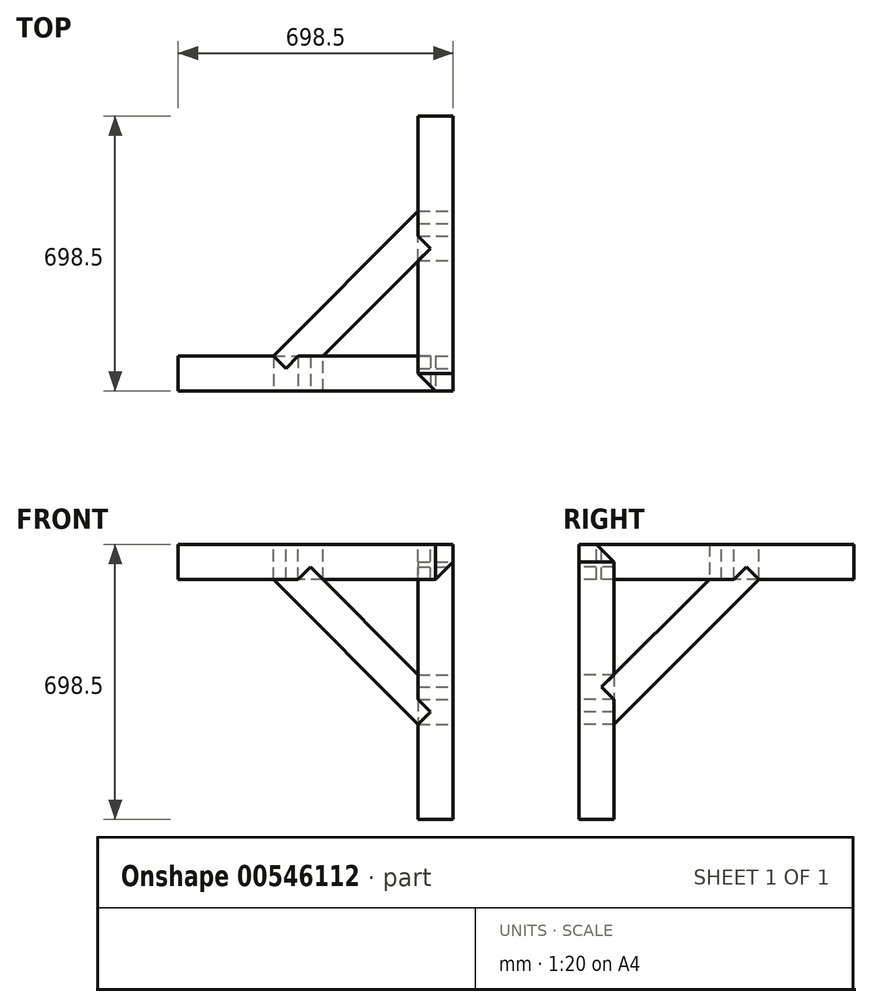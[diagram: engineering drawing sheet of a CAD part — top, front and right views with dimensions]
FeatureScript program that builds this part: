
annotation { "Feature Type Name" : "Feature", "Feature Type Description" : "" }
export const myFeature = defineFeature(function(context is Context, id is Id, definition is map)
    precondition{}
    {
        {
            var Q0;
            Q0=qCreatedBy(makeId("Top.planeOp"),FACE);
            var sketch = newSketch(context, id + "F0", { "sketchPlane" : qUnion([Q0])});
            skLineSegment(sketch, "E0.bottom", {"start": v(0, 0) * mm, "end": v(88.9, 0) * mm});
            skLineSegment(sketch, "E0.top", {"start": v(0, -88.9) * mm, "end": v(88.9, -88.9) * mm});
            skLineSegment(sketch, "E0.left", {"start": v(0, 0) * mm, "end": v(0, -88.9) * mm});
            skLineSegment(sketch, "E0.right", {"start": v(88.9, 0) * mm, "end": v(88.9, -88.9) * mm});
            skSolve(sketch);
        }
        {
            var Q0;
            Q0=makeQuery(id+"F0.imprint","IMPRINT",FACE,{"disambiguationData":[TD([[makeQuery(id+"F0.imprint","IMPRINT",EDGE,{"derivedFrom":sQuery(id+"F0.wireOp",EDGE,"E0.bottom")}),-1.0]])]});
            extrude(context, id + "F1", {"entities" : qUnion([Q0]), "depth" : 88.9 * mm, "offsetDistance" : 25.4 * mm});
        }
        {
            var Q0;
            Q0=makeQuery(id+"F1.opExtrude","CAP_FACE",FACE,{"disambiguationData":[OSD([sQuery(id+"F0.wireOp",EDGE,"E0.bottom"),sQuery(id+"F0.wireOp",EDGE,"E0.top"),sQuery(id+"F0.wireOp",EDGE,"E0.left"),sQuery(id+"F0.wireOp",EDGE,"E0.right")])],"isStart":false});
            var sketch = newSketch(context, id + "F2", { "sketchPlane" : qUnion([Q0])});
            skLineSegment(sketch, "E1", {"start": v(0, -44.45) * mm, "end": v(44.45, -88.9) * mm});
            skLineSegment(sketch, "E2.bottom", {"start": v(0, 0) * mm, "end": v(-609.6, 0) * mm});
            skLineSegment(sketch, "E2.top", {"start": v(0, -88.9) * mm, "end": v(-609.6, -88.9) * mm});
            skLineSegment(sketch, "E2.left", {"start": v(0, 0) * mm, "end": v(0, -44.45) * mm});
            skLineSegment(sketch, "E2.right", {"start": v(-609.6, 0) * mm, "end": v(-609.6, -88.9) * mm});
            skLineSegment(sketch, "E3", {"start": v(0, -44.45) * mm, "end": v(0, -88.9) * mm, "construction": true});
            skSolve(sketch);
        }
        {
            var Q0;
            Q0=makeQuery(id+"F1.opExtrude","SWEPT_FACE",FACE,{"disambiguationData":[OSD([sQuery(id+"F0.wireOp",EDGE,"E0.top")])]});
            var sketch = newSketch(context, id + "F3", { "sketchPlane" : qUnion([Q0])});
            skLineSegment(sketch, "E4", {"start": v(44.45, 0) * mm, "end": v(88.9, 44.45) * mm});
            skLineSegment(sketch, "E5.bottom", {"start": v(88.9, 0) * mm, "end": v(0, 0) * mm});
            skLineSegment(sketch, "E5.top", {"start": v(88.9, -609.6) * mm, "end": v(0, -609.6) * mm});
            skLineSegment(sketch, "E5.left", {"start": v(88.9, 0) * mm, "end": v(88.9, -609.6) * mm});
            skLineSegment(sketch, "E5.right", {"start": v(0, 0) * mm, "end": v(0, -609.6) * mm});
            skLineSegment(sketch, "E6", {"start": v(88.9, 0) * mm, "end": v(88.9, 44.45) * mm});
            skSolve(sketch);
        }
        {
            var Q0;
            Q0=makeQuery(id+"F1.opExtrude","SWEPT_FACE",FACE,{"disambiguationData":[OSD([sQuery(id+"F0.wireOp",EDGE,"E0.right")])]});
            var sketch = newSketch(context, id + "F4", { "sketchPlane" : qUnion([Q0])});
            skLineSegment(sketch, "E7", {"start": v(0, 44.45) * mm, "end": v(-44.45, 88.9) * mm});
            skLineSegment(sketch, "E8.bottom", {"start": v(0, 88.9) * mm, "end": v(609.6, 88.9) * mm});
            skLineSegment(sketch, "E8.top", {"start": v(0, 0) * mm, "end": v(609.6, 0) * mm});
            skLineSegment(sketch, "E8.left", {"start": v(0, 88.9) * mm, "end": v(0, 0) * mm});
            skLineSegment(sketch, "E8.right", {"start": v(609.6, 88.9) * mm, "end": v(609.6, 0) * mm});
            skSolve(sketch);
        }
        {
            var Q0;
            {var subQ0=sQuery(id+"F2.wireOp",EDGE,"E1");Q0=makeQuery(id+"F2.imprint","IMPRINT",FACE,{"disambiguationData":[TD([[makeQuery(id+"F2.imprint","IMPRINT",EDGE,{"derivedFrom":subQ0}),-1.0]])]});}
            var Q1;
            Q1=makeQuery(id+"F2.imprint","IMPRINT",FACE,{"disambiguationData":[TD([[makeQuery(id+"F2.imprint","IMPRINT",EDGE,{"derivedFrom":sQuery(id+"F2.wireOp",EDGE,"E2.bottom")}),1.0]])]});
            extrude(context, id + "F5", {"entities" : qUnion([Q0, Q1]), "oppositeDirection" : true, "depth" : 88.9 * mm, "offsetDistance" : 25.4 * mm});
        }
        {
            var Q0;
            {var subQ0=sQuery(id+"F3.wireOp",EDGE,"E4");Q0=makeQuery(id+"F3.imprint","IMPRINT",FACE,{"disambiguationData":[TD([[makeQuery(id+"F3.imprint","IMPRINT",EDGE,{"derivedFrom":subQ0}),-1.0]])]});}
            var Q1;
            Q1=makeQuery(id+"F3.imprint","IMPRINT",FACE,{"disambiguationData":[TD([[makeQuery(id+"F3.imprint","IMPRINT",EDGE,{"derivedFrom":sQuery(id+"F3.wireOp",EDGE,"E5.top")}),-1.0]])]});
            extrude(context, id + "F6", {"entities" : qUnion([Q0, Q1]), "oppositeDirection" : true, "depth" : 88.9 * mm, "offsetDistance" : 25.4 * mm});
        }
        {
            var Q0;
            {var subQ0=sQuery(id+"F4.wireOp",EDGE,"E7");Q0=makeQuery(id+"F4.imprint","IMPRINT",FACE,{"disambiguationData":[TD([[makeQuery(id+"F4.imprint","IMPRINT",EDGE,{"derivedFrom":subQ0}),-1.0]])]});}
            var Q1;
            {var subQ4=sQuery(id+"F4.wireOp",EDGE,"E8.bottom");Q1=makeQuery(id+"F4.imprint","IMPRINT",FACE,{"disambiguationData":[TD([[makeQuery(id+"F4.imprint","IMPRINT",EDGE,{"derivedFrom":subQ4}),-1.0]])]});}
            extrude(context, id + "F7", {"entities" : qUnion([Q0, Q1]), "oppositeDirection" : true, "depth" : 88.9 * mm, "offsetDistance" : 25.4 * mm});
        }
        {
            var Q0;
            Q0=makeQuery(id+"F5.opExtrude","SWEPT_BODY",BODY,{"disambiguationData":[OSD([sQuery(id+"F0.wireOp",EDGE,"E0.top"),sQuery(id+"F2.wireOp",EDGE,"E1"),sQuery(id+"F2.wireOp",EDGE,"E2.bottom"),sQuery(id+"F2.wireOp",EDGE,"E2.top"),sQuery(id+"F2.wireOp",EDGE,"E2.left"),sQuery(id+"F2.wireOp",EDGE,"E2.right")])]});
            var Q1;
            Q1=makeQuery(id+"F7.opExtrude","SWEPT_BODY",BODY,{"disambiguationData":[OSD([sQuery(id+"F0.wireOp",EDGE,"E0.right"),sQuery(id+"F4.wireOp",EDGE,"E7"),sQuery(id+"F4.wireOp",EDGE,"E8.bottom"),sQuery(id+"F4.wireOp",EDGE,"E8.top"),sQuery(id+"F4.wireOp",EDGE,"E8.left"),sQuery(id+"F4.wireOp",EDGE,"E8.right")])]});
            var Q2;
            Q2=makeQuery(id+"F6.opExtrude","SWEPT_BODY",BODY,{"disambiguationData":[OSD([sQuery(id+"F3.wireOp",EDGE,"E4"),sQuery(id+"F3.wireOp",EDGE,"E5.bottom"),sQuery(id+"F3.wireOp",EDGE,"E5.top"),sQuery(id+"F3.wireOp",EDGE,"E5.left"),sQuery(id+"F3.wireOp",EDGE,"E5.right"),sQuery(id+"F3.wireOp",EDGE,"E6")])]});
            var Q3;
            Q3=makeQuery(id+"F1.opExtrude","SWEPT_BODY",BODY,{"disambiguationData":[OSD([sQuery(id+"F0.wireOp",EDGE,"E0.bottom"),sQuery(id+"F0.wireOp",EDGE,"E0.top"),sQuery(id+"F0.wireOp",EDGE,"E0.left"),sQuery(id+"F0.wireOp",EDGE,"E0.right")])]});
            booleanBodies(context, id + "F8", {"operationType" : BooleanOperationType.SUBTRACTION, "tools" : qUnion([Q0, Q1, Q2]), "targets" : qUnion([Q3]), "keepTools" : true});
        }
        {
            var Q0;
            Q0=makeQuery(id+"F7.opExtrude","SWEPT_FACE",FACE,{"disambiguationData":[OSD([sQuery(id+"F0.wireOp",EDGE,"E0.right"),sQuery(id+"F4.wireOp",EDGE,"E8.bottom")])]});
            var sketch = newSketch(context, id + "F9", { "sketchPlane" : qUnion([Q0])});
            skLineSegment(sketch, "E9.0.2", {"start": v(0, 0) * mm, "end": v(-609.6, 0) * mm, "construction": true});
            skLineSegment(sketch, "E10", {"start": v(0, 0) * mm, "end": v(0, 609.6) * mm, "construction": true});
            skLineSegment(sketch, "E11", {"start": v(0, 304.8) * mm, "end": v(-304.8, 0) * mm, "construction": true});
            skLineSegment(sketch, "E12", {"start": v(-241.94, 0) * mm, "end": v(0, 241.94) * mm});
            skLineSegment(sketch, "E13", {"start": v(0, 367.66) * mm, "end": v(-367.66, 0) * mm});
            skLineSegment(sketch, "E14", {"start": v(0, 241.94) * mm, "end": v(31.43, 273.37) * mm});
            skLineSegment(sketch, "E15", {"start": v(31.43, 273.37) * mm, "end": v(0, 304.8) * mm});
            skLineSegment(sketch, "E16", {"start": v(-367.66, 0) * mm, "end": v(-336.23, -31.43) * mm});
            skLineSegment(sketch, "E17", {"start": v(-336.23, -31.43) * mm, "end": v(-304.8, 0) * mm});
            skLineSegment(sketch, "E18", {"start": v(-241.94, 0) * mm, "end": v(-304.8, 0) * mm});
            skLineSegment(sketch, "E19", {"start": v(0, 367.66) * mm, "end": v(0, 304.8) * mm});
            skSolve(sketch);
        }
        {
            var Q0;
            Q0=makeQuery(id+"F5.opExtrude","SWEPT_FACE",FACE,{"disambiguationData":[OSD([sQuery(id+"F0.wireOp",EDGE,"E0.top"),sQuery(id+"F2.wireOp",EDGE,"E2.top")])]});
            var sketch = newSketch(context, id + "F10", { "sketchPlane" : qUnion([Q0])});
            skLineSegment(sketch, "E20.0", {"start": v(0, 0) * mm, "end": v(0, -609.6) * mm, "construction": true});
            skLineSegment(sketch, "E21", {"start": v(0, 0) * mm, "end": v(-609.6, 0) * mm, "construction": true});
            skLineSegment(sketch, "E22", {"start": v(0, -304.8) * mm, "end": v(-304.8, 0) * mm, "construction": true});
            skLineSegment(sketch, "E23", {"start": v(0, -241.94) * mm, "end": v(-241.94, 0) * mm});
            skLineSegment(sketch, "E24", {"start": v(-367.66, 0) * mm, "end": v(0, -367.66) * mm});
            skLineSegment(sketch, "E25", {"start": v(-241.94, 0) * mm, "end": v(-273.37, 31.43) * mm});
            skLineSegment(sketch, "E26", {"start": v(-273.37, 31.43) * mm, "end": v(-304.8, 0) * mm});
            skLineSegment(sketch, "E27", {"start": v(-367.66, 0) * mm, "end": v(-304.8, 0) * mm});
            skLineSegment(sketch, "E28", {"start": v(0, -304.8) * mm, "end": v(31.43, -336.23) * mm});
            skLineSegment(sketch, "E29", {"start": v(31.43, -336.23) * mm, "end": v(0, -367.66) * mm});
            skLineSegment(sketch, "E30", {"start": v(0, -241.94) * mm, "end": v(0, -304.8) * mm});
            skSolve(sketch);
        }
        {
            var Q0;
            Q0=makeQuery(id+"F6.opExtrude","SWEPT_FACE",FACE,{"disambiguationData":[OSD([sQuery(id+"F3.wireOp",EDGE,"E5.left"),sQuery(id+"F3.wireOp",EDGE,"E6")])]});
            var sketch = newSketch(context, id + "F11", { "sketchPlane" : qUnion([Q0])});
            skLineSegment(sketch, "E31.0", {"start": v(0, 0) * mm, "end": v(609.6, 0) * mm, "construction": true});
            skLineSegment(sketch, "E32", {"start": v(0, 0) * mm, "end": v(0, -609.6) * mm, "construction": true});
            skLineSegment(sketch, "E33", {"start": v(304.8, 0) * mm, "end": v(0, -304.8) * mm, "construction": true});
            skLineSegment(sketch, "E34", {"start": v(0, -241.94) * mm, "end": v(241.94, 0) * mm});
            skLineSegment(sketch, "E35", {"start": v(241.94, 0) * mm, "end": v(304.8, 0) * mm});
            skLineSegment(sketch, "E36", {"start": v(0, -241.94) * mm, "end": v(-31.43, -273.37) * mm});
            skLineSegment(sketch, "E37", {"start": v(-31.43, -273.37) * mm, "end": v(0, -304.8) * mm});
            skLineSegment(sketch, "E38", {"start": v(0, -367.66) * mm, "end": v(367.66, 0) * mm});
            skLineSegment(sketch, "E39", {"start": v(367.66, 0) * mm, "end": v(336.23, 31.43) * mm});
            skLineSegment(sketch, "E40", {"start": v(336.23, 31.43) * mm, "end": v(304.8, 0) * mm});
            skSolve(sketch);
        }
        {
            var Q0;
            Q0 = qSketchRegion(id + "F9", true);
            extrude(context, id + "F12", {"entities" : qUnion([Q0]), "oppositeDirection" : true, "depth" : 88.9 * mm, "offsetDistance" : 25.4 * mm});
        }
        {
            var Q0;
            {var subQ1=sQuery(id+"F10.wireOp",EDGE,"E23");Q0=makeQuery(id+"F10.imprint","IMPRINT",FACE,{"disambiguationData":[TD([[makeQuery(id+"F10.imprint","IMPRINT",EDGE,{"derivedFrom":subQ1}),1.0]])]});}
            var Q1;
            {var subQ0=sQuery(id+"F10.wireOp",EDGE,"E25");Q1=makeQuery(id+"F10.imprint","IMPRINT",FACE,{"disambiguationData":[TD([[makeQuery(id+"F10.imprint","IMPRINT",EDGE,{"derivedFrom":subQ0}),1.0]])]});}
            extrude(context, id + "F13", {"entities" : qUnion([Q0, Q1]), "oppositeDirection" : true, "depth" : 88.9 * mm, "offsetDistance" : 25.4 * mm});
        }
        {
            var Q0;
            {var subQ1=sQuery(id+"F11.wireOp",EDGE,"E34");Q0=makeQuery(id+"F11.imprint","IMPRINT",FACE,{"disambiguationData":[TD([[makeQuery(id+"F11.imprint","IMPRINT",EDGE,{"derivedFrom":subQ1}),-1.0]])]});}
            var Q1;
            {var subQ0=sQuery(id+"F11.wireOp",EDGE,"E36");Q1=makeQuery(id+"F11.imprint","IMPRINT",FACE,{"disambiguationData":[TD([[makeQuery(id+"F11.imprint","IMPRINT",EDGE,{"derivedFrom":subQ0}),1.0]])]});}
            extrude(context, id + "F14", {"entities" : qUnion([Q0, Q1]), "oppositeDirection" : true, "depth" : 88.9 * mm, "offsetDistance" : 25.4 * mm});
        }
        {
            var Q0;
            Q0=makeQuery(id+"F13.opExtrude","SWEPT_BODY",BODY,{"disambiguationData":[OSD([sQuery(id+"F10.wireOp",EDGE,"E23"),sQuery(id+"F10.wireOp",EDGE,"E24"),sQuery(id+"F10.wireOp",EDGE,"E25"),sQuery(id+"F10.wireOp",EDGE,"E26"),sQuery(id+"F10.wireOp",EDGE,"E27"),sQuery(id+"F10.wireOp",EDGE,"E28"),sQuery(id+"F10.wireOp",EDGE,"E29"),sQuery(id+"F10.wireOp",EDGE,"E30")])]});
            var Q1;
            Q1=makeQuery(id+"F12.opExtrude","SWEPT_BODY",BODY,{"disambiguationData":[OSD([sQuery(id+"F9.wireOp",EDGE,"E12"),sQuery(id+"F9.wireOp",EDGE,"E13"),sQuery(id+"F9.wireOp",EDGE,"E14"),sQuery(id+"F9.wireOp",EDGE,"E15"),sQuery(id+"F9.wireOp",EDGE,"E16"),sQuery(id+"F9.wireOp",EDGE,"E17"),sQuery(id+"F9.wireOp",EDGE,"E18"),sQuery(id+"F9.wireOp",EDGE,"E19")])]});
            var Q2;
            Q2=makeQuery(id+"F14.opExtrude","SWEPT_BODY",BODY,{"disambiguationData":[OSD([sQuery(id+"F3.wireOp",EDGE,"E5.left"),sQuery(id+"F3.wireOp",EDGE,"E6"),sQuery(id+"F11.wireOp",EDGE,"E34"),sQuery(id+"F11.wireOp",EDGE,"E35"),sQuery(id+"F11.wireOp",EDGE,"E36"),sQuery(id+"F11.wireOp",EDGE,"E37"),sQuery(id+"F11.wireOp",EDGE,"E38"),sQuery(id+"F11.wireOp",EDGE,"E39"),sQuery(id+"F11.wireOp",EDGE,"E40")])]});
            var Q3;
            Q3=makeQuery(id+"F6.opExtrude","SWEPT_BODY",BODY,{"disambiguationData":[OSD([sQuery(id+"F3.wireOp",EDGE,"E4"),sQuery(id+"F3.wireOp",EDGE,"E5.bottom"),sQuery(id+"F3.wireOp",EDGE,"E5.top"),sQuery(id+"F3.wireOp",EDGE,"E5.left"),sQuery(id+"F3.wireOp",EDGE,"E5.right"),sQuery(id+"F3.wireOp",EDGE,"E6")])]});
            var Q4;
            Q4=makeQuery(id+"F5.opExtrude","SWEPT_BODY",BODY,{"disambiguationData":[OSD([sQuery(id+"F0.wireOp",EDGE,"E0.top"),sQuery(id+"F2.wireOp",EDGE,"E1"),sQuery(id+"F2.wireOp",EDGE,"E2.bottom"),sQuery(id+"F2.wireOp",EDGE,"E2.top"),sQuery(id+"F2.wireOp",EDGE,"E2.left"),sQuery(id+"F2.wireOp",EDGE,"E2.right")])]});
            var Q5;
            Q5=makeQuery(id+"F7.opExtrude","SWEPT_BODY",BODY,{"disambiguationData":[OSD([sQuery(id+"F0.wireOp",EDGE,"E0.right"),sQuery(id+"F4.wireOp",EDGE,"E7"),sQuery(id+"F4.wireOp",EDGE,"E8.bottom"),sQuery(id+"F4.wireOp",EDGE,"E8.top"),sQuery(id+"F4.wireOp",EDGE,"E8.left"),sQuery(id+"F4.wireOp",EDGE,"E8.right")])]});
            booleanBodies(context, id + "F15", {"operationType" : BooleanOperationType.SUBTRACTION, "tools" : qUnion([Q0, Q1, Q2]), "targets" : qUnion([Q3, Q4, Q5]), "keepTools" : true});
        }
    });
